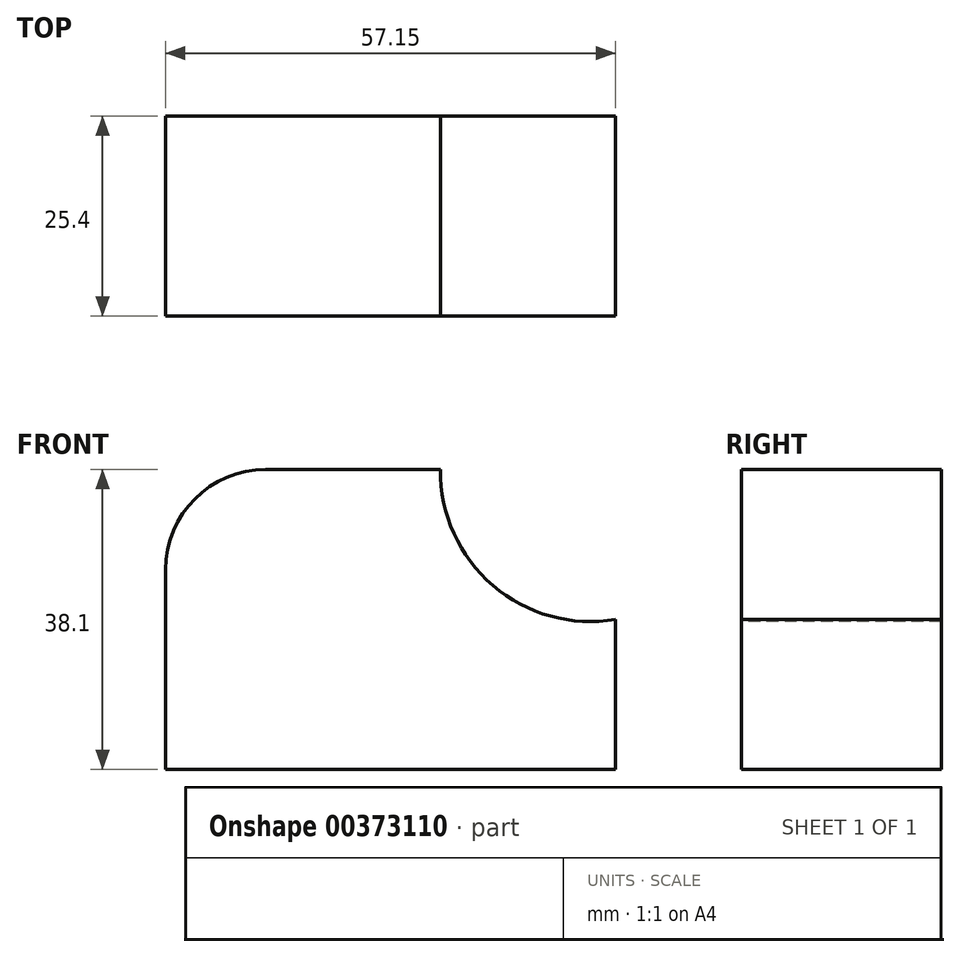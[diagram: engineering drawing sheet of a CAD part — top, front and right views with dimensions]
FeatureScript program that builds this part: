
annotation { "Feature Type Name" : "Feature", "Feature Type Description" : "" }
export const myFeature = defineFeature(function(context is Context, id is Id, definition is map)
    precondition{}
    {
        {
            var Q0;
            Q0=qCreatedBy(makeId("Front.planeOp"),FACE);
            var sketch = newSketch(context, id + "F0", { "sketchPlane" : qUnion([Q0])});
            skLineSegment(sketch, "E0", {"start": v(0, 0) * mm, "end": v(0, 38.1) * mm});
            skLineSegment(sketch, "E1", {"start": v(0, 38.1) * mm, "end": v(57.15, 38.1) * mm});
            skLineSegment(sketch, "E2", {"start": v(57.15, 38.1) * mm, "end": v(57.15, 0) * mm});
            skLineSegment(sketch, "E3", {"start": v(57.15, 0) * mm, "end": v(0, 0) * mm});
            skSolve(sketch);
        }
        {
            var Q0;
            Q0 = qSketchRegion(id + "F0", true);
            extrude(context, id + "F1", {"entities" : qUnion([Q0]), "depth" : 25.4 * mm});
        }
        {
            var Q0;
            Q0=makeQuery(id+"F1.opExtrude","SWEPT_EDGE",EDGE,{"disambiguationData":[OSD([sQuery(id+"F0.wireOp",EDGE,"E0"),sQuery(id+"F0.wireOp",EDGE,"E1")])]});
            fillet(context, id + "F2", {"entities" : qUnion([Q0]), "radius" : 12.7 * mm, "tangentPropagation" : true, "allowEdgeOverflow" : false});
        }
        {
            var Q0;
            Q0=makeQuery(id+"F1.opExtrude","CAP_FACE",FACE,{"disambiguationData":[OSD([sQuery(id+"F0.wireOp",EDGE,"E0"),sQuery(id+"F0.wireOp",EDGE,"E1"),sQuery(id+"F0.wireOp",EDGE,"E2"),sQuery(id+"F0.wireOp",EDGE,"E3")])],"isStart":false});
            var sketch = newSketch(context, id + "F3", { "sketchPlane" : qUnion([Q0])});
            skArc(sketch, "E4", {"start": v(34.93, 38.1) * mm, "mid": v(41.58, 23.37) * mm, "end": v(57.15, 19.05) * mm});
            skLineSegment(sketch, "E5", {"start": v(34.93, 38.1) * mm, "end": v(57.15, 38.1) * mm});
            skLineSegment(sketch, "E6", {"start": v(57.15, 38.1) * mm, "end": v(57.15, 19.05) * mm});
            skSolve(sketch);
        }
        {
            var Q0;
            Q0 = qSketchRegion(id + "F3", true);
            extrude(context, id + "F4", {"entities" : qUnion([Q0]), "operationType" : NewBodyOperationType.REMOVE, "oppositeDirection" : true, "depth" : 25.4 * mm});
        }
    });
